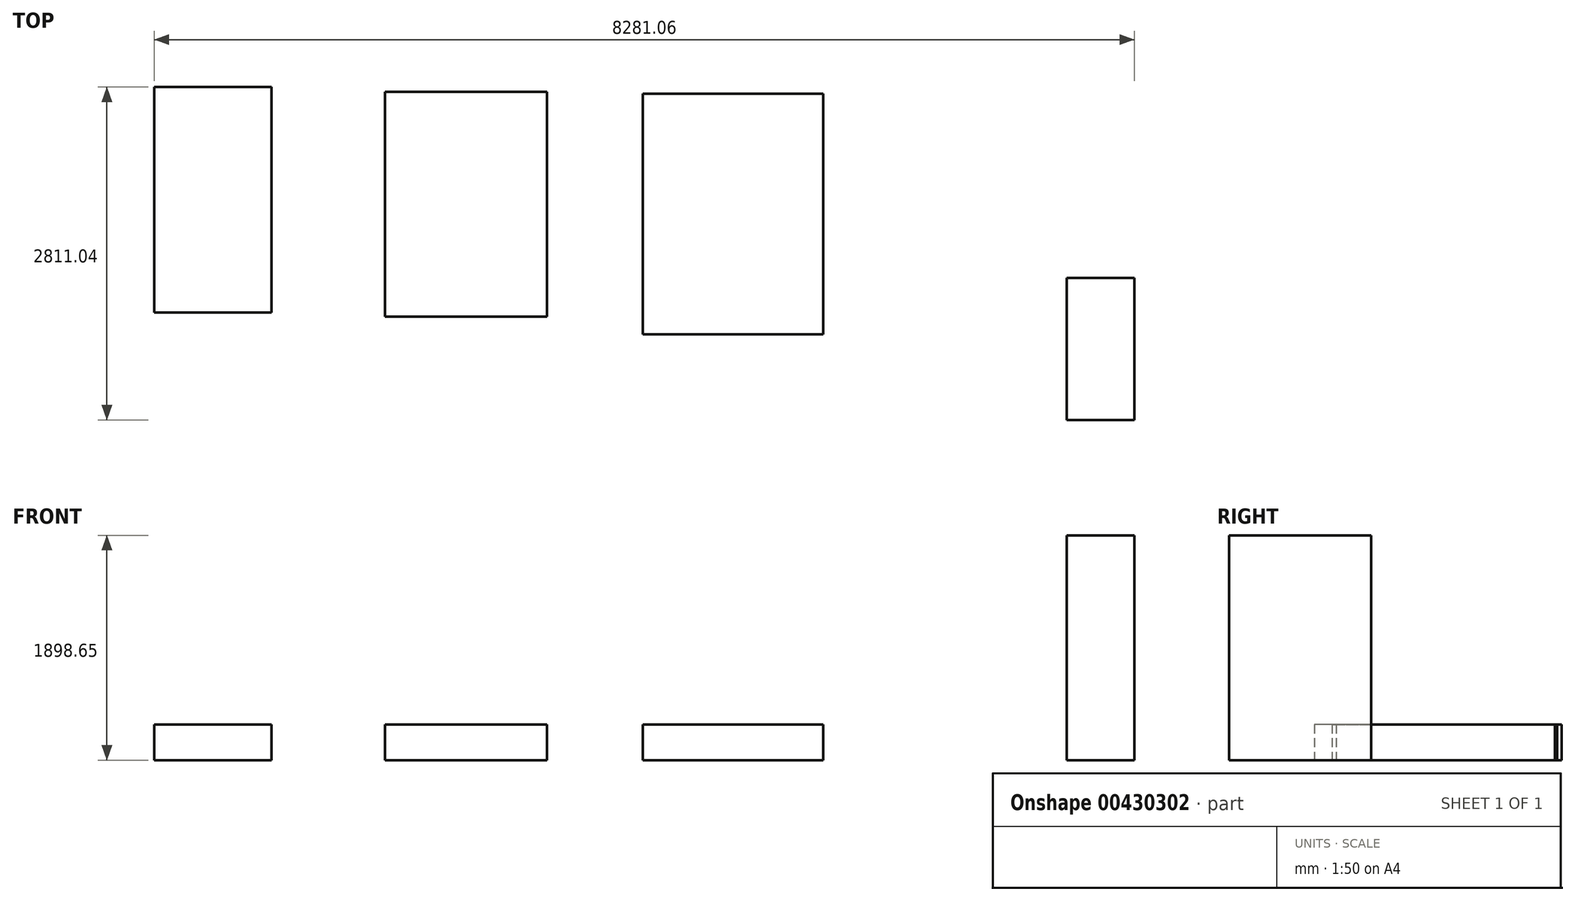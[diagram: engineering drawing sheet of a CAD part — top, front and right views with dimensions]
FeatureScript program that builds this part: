
annotation { "Feature Type Name" : "Feature", "Feature Type Description" : "" }
export const myFeature = defineFeature(function(context is Context, id is Id, definition is map)
    precondition{}
    {
        {
            var Q0;
            Q0=qCreatedBy(makeId("Top.planeOp"),FACE);
            var sketch = newSketch(context, id + "F0", { "sketchPlane" : qUnion([Q0])});
            skLineSegment(sketch, "E0.bottom", {"start": v(-800.95, 917.1) * mm, "end": v(723.05, 917.1) * mm});
            skLineSegment(sketch, "E0.top", {"start": v(-800.95, -1114.9) * mm, "end": v(723.05, -1114.9) * mm});
            skLineSegment(sketch, "E0.left", {"start": v(-800.95, 917.1) * mm, "end": v(-800.95, -1114.9) * mm});
            skLineSegment(sketch, "E0.right", {"start": v(723.05, 917.1) * mm, "end": v(723.05, -1114.9) * mm});
            skSolve(sketch);
        }
        {
            var Q0;
            Q0 = qSketchRegion(id + "F0", true);
            extrude(context, id + "F1", {"entities" : qUnion([Q0]), "depth" : 300 * mm});
        }
        {
            var Q0;
            Q0=qCreatedBy(makeId("Top.planeOp"),FACE);
            var sketch = newSketch(context, id + "F2", { "sketchPlane" : qUnion([Q0])});
            skLineSegment(sketch, "E1.bottom", {"start": v(-1610.43, -964.86) * mm, "end": v(-2980.43, -964.86) * mm});
            skLineSegment(sketch, "E1.top", {"start": v(-1610.43, 935.14) * mm, "end": v(-2980.43, 935.14) * mm});
            skLineSegment(sketch, "E1.left", {"start": v(-1610.43, -964.86) * mm, "end": v(-1610.43, 935.14) * mm});
            skLineSegment(sketch, "E1.right", {"start": v(-2980.43, -964.86) * mm, "end": v(-2980.43, 935.14) * mm});
            skSolve(sketch);
        }
        {
            var Q0;
            Q0=makeQuery(id+"F2.imprint","IMPRINT",FACE,{"disambiguationData":[TD([[makeQuery(id+"F2.imprint","IMPRINT",EDGE,{"derivedFrom":sQuery(id+"F2.wireOp",EDGE,"E1.bottom")}),-1.0]])]});
            extrude(context, id + "F3", {"entities" : qUnion([Q0]), "depth" : 300 * mm});
        }
        {
            var Q0;
            Q0=qCreatedBy(makeId("Top.planeOp"),FACE);
            var sketch = newSketch(context, id + "F4", { "sketchPlane" : qUnion([Q0])});
            skLineSegment(sketch, "E2.bottom", {"start": v(-3938.83, -929.77) * mm, "end": v(-4929.43, -929.77) * mm});
            skLineSegment(sketch, "E2.top", {"start": v(-3938.83, 975.23) * mm, "end": v(-4929.43, 975.23) * mm});
            skLineSegment(sketch, "E2.left", {"start": v(-3938.83, -929.77) * mm, "end": v(-3938.83, 975.23) * mm});
            skLineSegment(sketch, "E2.right", {"start": v(-4929.43, -929.77) * mm, "end": v(-4929.43, 975.23) * mm});
            skSolve(sketch);
        }
        {
            var Q0;
            Q0=makeQuery(id+"F4.imprint","IMPRINT",FACE,{"disambiguationData":[TD([[makeQuery(id+"F4.imprint","IMPRINT",EDGE,{"derivedFrom":sQuery(id+"F4.wireOp",EDGE,"E2.bottom")}),-1.0]])]});
            extrude(context, id + "F5", {"entities" : qUnion([Q0]), "depth" : 300 * mm});
        }
        {
            var Q0;
            Q0=qCreatedBy(makeId("Top.planeOp"),FACE);
            var sketch = newSketch(context, id + "F6", { "sketchPlane" : qUnion([Q0])});
            skLineSegment(sketch, "E3.bottom", {"start": v(2780.13, -635.66) * mm, "end": v(3351.63, -635.66) * mm});
            skLineSegment(sketch, "E3.top", {"start": v(2780.13, -1835.81) * mm, "end": v(3351.63, -1835.81) * mm});
            skLineSegment(sketch, "E3.left", {"start": v(2780.13, -635.66) * mm, "end": v(2780.13, -1835.81) * mm});
            skLineSegment(sketch, "E3.right", {"start": v(3351.63, -635.66) * mm, "end": v(3351.63, -1835.81) * mm});
            skSolve(sketch);
        }
        {
            var Q0;
            Q0 = qSketchRegion(id + "F6", true);
            extrude(context, id + "F7", {"entities" : qUnion([Q0]), "depth" : 1898.65 * mm});
        }
    });
